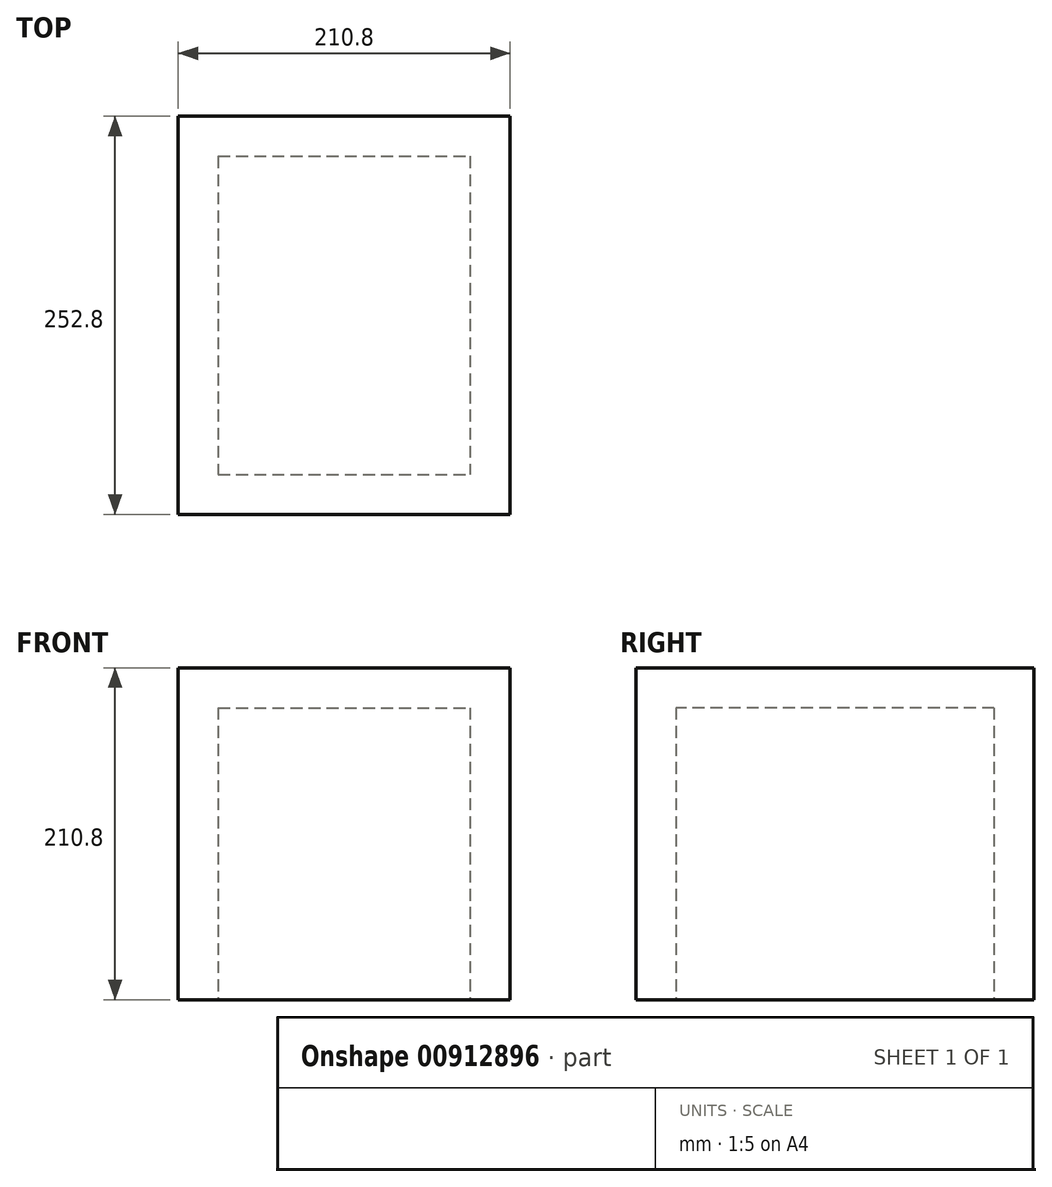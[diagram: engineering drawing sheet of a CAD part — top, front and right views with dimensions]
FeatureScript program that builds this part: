
annotation { "Feature Type Name" : "Feature", "Feature Type Description" : "" }
export const myFeature = defineFeature(function(context is Context, id is Id, definition is map)
    precondition{}
    {
        {
            var Q0;
            Q0=qCreatedBy(makeId("Top.planeOp"),FACE);
            var sketch = newSketch(context, id + "F0", { "sketchPlane" : qUnion([Q0])});
            skLineSegment(sketch, "E0.bottom", {"start": v(-176.71, 101.84) * mm, "end": v(34.09, 101.84) * mm});
            skLineSegment(sketch, "E0.top", {"start": v(-176.71, -150.96) * mm, "end": v(34.09, -150.96) * mm});
            skLineSegment(sketch, "E0.left", {"start": v(-176.71, 101.84) * mm, "end": v(-176.71, -150.96) * mm});
            skLineSegment(sketch, "E0.right", {"start": v(34.09, 101.84) * mm, "end": v(34.09, -150.96) * mm});
            skSolve(sketch);
        }
        {
            var Q0;
            Q0=makeQuery(id+"F0.imprint","IMPRINT",FACE,{"disambiguationData":[TD([[makeQuery(id+"F0.imprint","IMPRINT",EDGE,{"derivedFrom":sQuery(id+"F0.wireOp",EDGE,"E0.bottom")}),-1.0]])]});
            extrude(context, id + "F1", {"entities" : qUnion([Q0]), "depth" : (160 + 25.4 + 25.4) * mm, "offsetDistance" : 25 * mm});
        }
        {
            var Q0;
            Q0=makeQuery(id+"F1.opExtrude","CAP_FACE",FACE,{"disambiguationData":[OSD([sQuery(id+"F0.wireOp",EDGE,"E0.bottom"),sQuery(id+"F0.wireOp",EDGE,"E0.top"),sQuery(id+"F0.wireOp",EDGE,"E0.left"),sQuery(id+"F0.wireOp",EDGE,"E0.right")])],"isStart":true});
            shell(context, id + "F2", {"entities" : qUnion([Q0]), "thickness" : 25.4 * mm});
        }
    });
